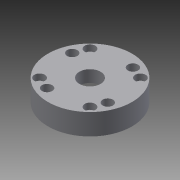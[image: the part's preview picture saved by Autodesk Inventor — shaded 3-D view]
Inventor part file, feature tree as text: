
AUTODESK INVENTOR PART (.ipt)
format: ipt  version: 2014 SP2 (Build 180246200, 246)  size: 285,184 bytes
history: native  units: in
note: dims shown in document units (in); Inventor stores cm internally (conversion verified against a paired STEP export)
features: other x322, sketch x10, hole x6, revolve x4, thread x1, pattern_linear x1
ambient origin geometry x8: Origin, YZ Plane, XZ Plane, XY Plane, X Axis, Y Axis, Z Axis, Center Point
bodies: Solid1 (feature_tree)
feature tree (344):
  revolve  "Revolution1"  Angle=360.0deg
  revolve  "Revolution2"  Angle=360.0deg
  thread  "Thread1"  [1 undecoded]
  revolve  "Revolution3"  [1 undecoded]
  hole  "Hole1"  [1 undecoded]
  hole  "Hole2"  [1 undecoded]
  hole  "Hole3"  [1 undecoded]
  hole  "Hole4"  [1 undecoded]
  hole  "Hole5"  [1 undecoded]
  revolve  "Revolution4"  [1 undecoded]
  hole  "Hole6"  [1 undecoded]
  pattern_linear  "Rectangular Pattern1"  [2 undecoded]
  other  "a1_XY"
  other  "a1_YZ"
  other  "a1_ZX"
  other  "a1_X"
  other  "a1_Y"
  other  "a1_Z"
  other  "a1_Center"
  other  "a2_XY"
  other  "a2_YZ"
  other  "a2_ZX"
  other  "a2_X"
  other  "a2_Y"
  other  "a2_Z"
  other  "a2_Center"
  other  "ab_tr1_XY"
  other  "ab_tr1_YZ"
  other  "ab_tr1_ZX"
  other  "ab_tr1_X"
  other  "ab_tr1_Y"
  other  "ab_tr1_Z"
  other  "ab_tr1_Center"
  other  "ab_tr2_XY"
  other  "ab_tr2_YZ"
  other  "ab_tr2_ZX"
  other  "ab_tr2_X"
  other  "ab_tr2_Y"
  other  "ab_tr2_Z"
  other  "ab_tr2_Center"
  other  "ab_tr3_XY"
  other  "ab_tr3_YZ"
  other  "ab_tr3_ZX"
  other  "ab_tr3_X"
  other  "ab_tr3_Y"
  other  "ab_tr3_Z"
  other  "ab_tr3_Center"
  other  "ab_tr4_XY"
  other  "ab_tr4_YZ"
  other  "ab_tr4_ZX"
  other  "ab_tr4_X"
  other  "ab_tr4_Y"
  other  "ab_tr4_Z"
  other  "ab_tr4_Center"
  other  "ar3_XY"
  other  "ar3_YZ"
  other  "ar3_ZX"
  other  "ar3_X"
  other  "ar3_Y"
  other  "ar3_Z"
  other  "ar3_Center"
  other  "ar4_XY"
  other  "ar4_YZ"
  other  "ar4_ZX"
  other  "ar4_X"
  other  "ar4_Y"
  other  "ar4_Z"
  other  "ar4_Center"
  other  "ar5_XY"
  other  "ar5_YZ"
  other  "ar5_ZX"
  other  "ar5_X"
  other  "ar5_Y"
  other  "ar5_Z"
  other  "ar5_Center"
  other  "ar6_XY"
  other  "ar6_YZ"
  other  "ar6_ZX"
  other  "ar6_X"
  other  "ar6_Y"
  other  "ar6_Z"
  other  "ar6_Center"
  other  "b1_XY"
  other  "b1_YZ"
  other  "b1_ZX"
  other  "b1_X"
  other  "b1_Y"
  other  "b1_Z"
  other  "b1_Center"
  other  "c11_XY"
  other  "c11_YZ"
  other  "c11_ZX"
  other  "c11_X"
  other  "c11_Y"
  other  "c11_Z"
  other  "c11_Center"
  other  "c22_XY"
  other  "c22_YZ"
  other  "c22_ZX"
  other  "c22_X"
  other  "c22_Y"
  other  "c22_Z"
  other  "c22_Center"
  other  "d11_XY"
  other  "d11_YZ"
  other  "d11_ZX"
  other  "d11_X"
  other  "d11_Y"
  other  "d11_Z"
  other  "d11_Center"
  other  "d22_XY"
  other  "d22_YZ"
  other  "d22_ZX"
  other  "d22_X"
  other  "d22_Y"
  other  "d22_Z"
  other  "d22_Center"
  other  "j_XY"
  other  "j_YZ"
  other  "j_ZX"
  other  "j_X"
  other  "j_Y"
  other  "j_Z"
  other  "j_Center"
  other  "k1_XY"
  other  "k1_YZ"
  other  "k1_ZX"
  other  "k1_X"
  other  "k1_Y"
  other  "k1_Z"
  other  "k1_Center"
  other  "k2_XY"
  other  "k2_YZ"
  other  "k2_ZX"
  other  "k2_X"
  other  "k2_Y"
  other  "k2_Z"
  other  "k2_Center"
  other  "nut_XY"
  other  "nut_YZ"
  other  "nut_ZX"
  other  "nut_X"
  other  "nut_Y"
  other  "nut_Z"
  other  "nut_Center"
  other  "po1_XY"
  other  "po1_YZ"
  other  "po1_ZX"
  other  "po1_X"
  other  "po1_Y"
  other  "po1_Z"
  other  "po1_Center"
  other  "po2_XY"
  other  "po2_YZ"
  other  "po2_ZX"
  other  "po2_X"
  other  "po2_Y"
  other  "po2_Z"
  other  "po2_Center"
  other  "po3_XY"
  other  "po3_YZ"
  other  "po3_ZX"
  other  "po3_X"
  other  "po3_Y"
  other  "po3_Z"
  other  "po3_Center"
  other  "po4_XY"
  other  "po4_YZ"
  other  "po4_ZX"
  other  "po4_X"
  other  "po4_Y"
  other  "po4_Z"
  other  "po4_Center"
  other  "r7_XY"
  other  "r7_YZ"
  other  "r7_ZX"
  other  "r7_X"
  other  "r7_Y"
  other  "r7_Z"
  other  "r7_Center"
  other  "r71_XY"
  other  "r71_YZ"
  other  "r71_ZX"
  other  "r71_X"
  other  "r71_Y"
  other  "r71_Z"
  other  "r71_Center"
  other  "r72_XY"
  other  "r72_YZ"
  other  "r72_ZX"
  other  "r72_X"
  other  "r72_Y"
  other  "r72_Z"
  other  "r72_Center"
  other  "r73_XY"
  other  "r73_YZ"
  other  "r73_ZX"
  other  "r73_X"
  other  "r73_Y"
  other  "r73_Z"
  other  "r73_Center"
  other  "rg_XY"
  other  "rg_YZ"
  other  "rg_ZX"
  other  "rg_X"
  other  "rg_Y"
  other  "rg_Z"
  other  "rg_Center"
  other  "rh_XY"
  other  "rh_YZ"
  other  "rh_ZX"
  other  "rh_X"
  other  "rh_Y"
  other  "rh_Z"
  other  "rh_Center"
  other  "rs_1_XY"
  other  "rs_1_YZ"
  other  "rs_1_ZX"
  other  "rs_1_X"
  other  "rs_1_Y"
  other  "rs_1_Z"
  other  "rs_1_Center"
  other  "rs_2_XY"
  other  "rs_2_YZ"
  other  "rs_2_ZX"
  other  "rs_2_X"
  other  "rs_2_Y"
  other  "rs_2_Z"
  other  "rs_2_Center"
  other  "rs_3_XY"
  other  "rs_3_YZ"
  other  "rs_3_ZX"
  other  "rs_3_X"
  other  "rs_3_Y"
  other  "rs_3_Z"
  other  "rs_3_Center"
  other  "rs_4_XY"
  other  "rs_4_YZ"
  other  "rs_4_ZX"
  other  "rs_4_X"
  other  "rs_4_Y"
  other  "rs_4_Z"
  other  "rs_4_Center"
  other  "sc1_XY"
  other  "sc1_YZ"
  other  "sc1_ZX"
  other  "sc1_X"
  other  "sc1_Y"
  other  "sc1_Z"
  other  "sc1_Center"
  other  "sc2_XY"
  other  "sc2_YZ"
  other  "sc2_ZX"
  other  "sc2_X"
  other  "sc2_Y"
  other  "sc2_Z"
  other  "sc2_Center"
  other  "sc3_XY"
  other  "sc3_YZ"
  other  "sc3_ZX"
  other  "sc3_X"
  other  "sc3_Y"
  other  "sc3_Z"
  other  "sc3_Center"
  other  "sc4_XY"
  other  "sc4_YZ"
  other  "sc4_ZX"
  other  "sc4_X"
  other  "sc4_Y"
  other  "sc4_Z"
  other  "sc4_Center"
  other  "to_dummy_XY"
  other  "to_dummy_YZ"
  other  "to_dummy_ZX"
  other  "to_dummy_X"
  other  "to_dummy_Y"
  other  "to_dummy_Z"
  other  "to_dummy_Center"
  other  "to_nut_XY"
  other  "to_nut_YZ"
  other  "to_nut_ZX"
  other  "to_nut_X"
  other  "to_nut_Y"
  other  "to_nut_Z"
  other  "to_nut_Center"
  other  "to_rod_XY"
  other  "to_rod_YZ"
  other  "to_rod_ZX"
  other  "to_rod_X"
  other  "to_rod_Y"
  other  "to_rod_Z"
  other  "to_rod_Center"
  other  "to_tube_XY"
  other  "to_tube_YZ"
  other  "to_tube_ZX"
  other  "to_tube_X"
  other  "to_tube_Y"
  other  "to_tube_Z"
  other  "to_tube_Center"
  other  "to_wiper_XY"
  other  "to_wiper_YZ"
  other  "to_wiper_ZX"
  other  "to_wiper_X"
  other  "to_wiper_Y"
  other  "to_wiper_Z"
  other  "to_wiper_Center"
  other  "track1_XY"
  other  "track1_YZ"
  other  "track1_ZX"
  other  "track1_X"
  other  "track1_Y"
  other  "track1_Z"
  other  "track1_Center"
  other  "track2_XY"
  other  "track2_YZ"
  other  "track2_ZX"
  other  "track2_X"
  other  "track2_Y"
  other  "track2_Z"
  other  "track2_Center"
  other  "track3_XY"
  other  "track3_YZ"
  other  "track3_ZX"
  other  "track3_X"
  other  "track3_Y"
  other  "track3_Z"
  other  "track3_Center"
  other  "track4_XY"
  other  "track4_YZ"
  other  "track4_ZX"
  other  "track4_X"
  other  "track4_Y"
  other  "track4_Z"
  other  "track4_Center"
  sketch  "Sketch_1"  dims[d0=360.0deg d1=360.0deg]
  sketch  "Sketch_84"  dims[d54=0.0in d55=0.0in d56=0.0in d57=0.0in d58=0.0in d59=0.0in d60=0.0in d61=0.0in d62=0.0in d63=0.0in d64=0.0in d65=0.0in d66=0.0in d67=0.0in d68=0.0in d69=0.0in d70=0.0in d71=0.0in d72=0.0in d73=0.0in d74=0.0in d75=0.0in d76=0.0in d77=0.0in d78=0.0in d79=0.0in d80=0.0in d81=0.0in d82=0.0in d83=0.0in d84=0.0in d85=0.0in d86=0.0in d87=0.0in]
  sketch  "Sketch_85"
  sketch  "Sketch4"  dims[d2=0.3302in d3=0.0in d4=360.0deg]
  sketch  "Sketch5"  dims[d5=0.156in d6=0.75in d7=0.25in d8=0.148in d9=0.5635in d10=0.5in d11=0.0in]
  sketch  "Sketch6"  dims[d12=0.156in d13=0.75in d14=0.25in d15=0.148in d16=0.5635in d17=0.5in d18=0.0in]
  sketch  "Sketch7"  dims[d19=0.156in d20=0.75in d21=0.25in d22=0.148in d23=0.5635in d24=0.5in d25=0.0in]
  sketch  "Sketch8"  dims[d26=0.156in d27=0.75in d28=0.25in d29=0.148in d30=0.5635in d31=0.5in d32=0.0in]
  sketch  "Sketch_9"  dims[d33=0.502in d34=0.75in d35=0.375in d36=0.25in d37=0.5635in d38=0.5in d39=0.0in d40=360.0deg]
  sketch  "Sketch10"  dims[d41=0.154in d42=0.75in d43=0.242in d44=0.18in d45=0.5635in d46=0.5in d47=0.0in d48=0.7874in d50=1.1003in d51=0.7874in d53=1.1003in]
note: 11 required parameter values undecoded (feature->parameter linkage not recoverable at this tier; creation-order binding heuristic only, values carry confidence <= 0.55)